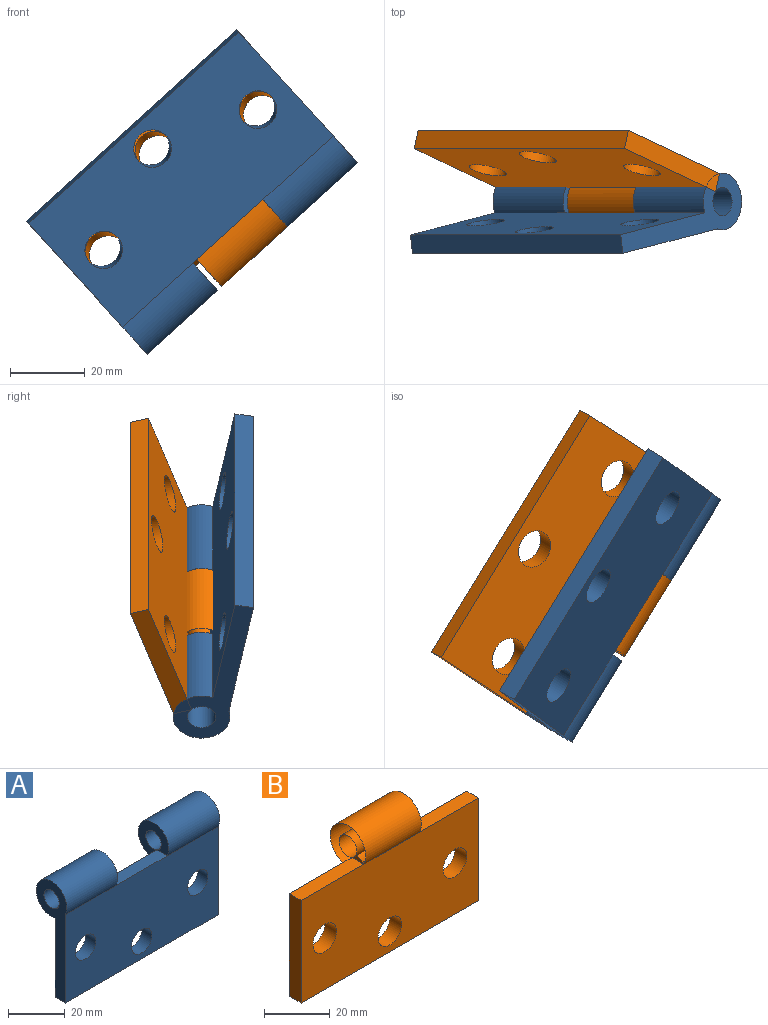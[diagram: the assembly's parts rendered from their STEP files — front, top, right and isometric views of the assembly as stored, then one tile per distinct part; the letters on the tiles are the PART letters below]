
ASSEMBLY  parts=2 mates=1
PART A: 15 faces, bbox 76.2x15.2x49.1 mm
  f0: plane 25.4x5.08mm, normal (0,0,1), area 129mm2, adj f4,f5,f8,f11
  f1: plane 49.11x15.24mm, normal (-1,0,0), area 317mm2, adj f2,f4,f5,f9,f10
  f2: plane 76.2x5.08mm, normal (0,0,-1), area 387.1mm2, adj f1,f3,f4,f5
  f3: plane 49.11x15.24mm, normal (1,0,0), area 317mm2, adj f2,f4,f5,f6,f7
  f4: plane 76.2x38.1mm, normal (0,-1,0), area 2660mm2, adj f0,f1,f2,f3,f7,f9,f12,f13
  f5: plane 76.2x38.1mm, normal (0,1,0), area 2455.2mm2, adj f0,f1,f2,f3,f7,f8,f9,f11
  f6: cylinder r=3.81mm len=25.4mm, axis (1,0,0), area 608mm2, adj f3,f8
  f7: cylinder r=7.62mm len=25.4mm, axis (1,0,0), area 1046mm2, adj f3,f4,f5,f8
  f8: plane 15.24x15.24mm, normal (-1,0,0), area 123.4mm2, adj f0,f5,f6,f7
  f9: cylinder r=7.62mm len=25.4mm, axis (-1,0,0), area 1046mm2, adj f1,f4,f5,f11
  f10: cylinder r=3.81mm len=25.4mm, axis (-1,0,0), area 608mm2, adj f1,f11
  f11: plane 15.24x15.24mm, normal (1,0,0), area 123.4mm2, adj f0,f5,f9,f10
  f12: cylinder r=5.08mm len=10.16mm, axis (0,-1,0), area 162.1mm2, adj f4,f5
  f13: cylinder r=5.08mm len=10.16mm, axis (0,-1,0), area 162.1mm2, adj f4,f5
  f14: cylinder r=5.08mm len=10.16mm, axis (0,-1,0), area 162.1mm2, adj f4,f5
PART B: 14 faces, bbox 76.2x15.2x49.1 mm
  f0: plane 26.92x5.08mm, normal (0,0,1), area 136.8mm2, adj f1,f2,f6,f9
  f1: plane 76.2x38.1mm, normal (0,1,0), area 2563.8mm2, adj f0,f2,f3,f4,f5,f8,f9,f10
  f2: plane 38.1x5.08mm, normal (-1,0,0), area 193.5mm2, adj f0,f1,f3,f6
  f3: plane 76.2x5.08mm, normal (0,0,-1), area 387.1mm2, adj f1,f2,f4,f6
  f4: plane 38.1x5.08mm, normal (1,0,0), area 193.5mm2, adj f1,f3,f5,f6
  f5: plane 25.4x5.08mm, normal (0,0,1), area 129mm2, adj f1,f4,f6,f10
  f6: plane 76.2x38.1mm, normal (0,-1,0), area 2660mm2, adj f0,f2,f3,f4,f5,f8,f11,f12
  f7: cylinder r=3.81mm len=23.88mm, axis (1,0,0), area 571.6mm2, adj f9,f10
  f8: cylinder r=7.62mm len=23.88mm, axis (1,0,0), area 983.2mm2, adj f1,f6,f9,f10
  f9: plane 15.24x15.24mm, normal (-1,0,0), area 123.4mm2, adj f0,f1,f7,f8
  f10: plane 15.24x15.24mm, normal (1,0,0), area 123.4mm2, adj f1,f5,f7,f8
  f11: cylinder r=5.08mm len=10.16mm, axis (0,-1,0), area 162.1mm2, adj f1,f6
  f12: cylinder r=5.08mm len=10.16mm, axis (0,-1,0), area 162.1mm2, adj f1,f6
  f13: cylinder r=5.08mm len=10.16mm, axis (0,-1,0), area 162.1mm2, adj f1,f6
PLACE A rot(axis=(-0.03,1,0.09),137.9deg) t=(-51.26,-35.92,46.59)mm
PLACE B rot(axis=(0.93,-0.06,0.36),163.6deg) t=(-42.65,-24.04,69.94)mm
MATE revolute A.f6 <-> B.f7  axis (-0.74,0,-0.67) through (-19.22,-32.49,63.05)mm
